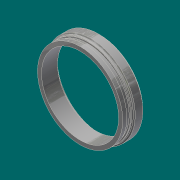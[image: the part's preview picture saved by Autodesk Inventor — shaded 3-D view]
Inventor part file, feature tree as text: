
AUTODESK INVENTOR PART (.ipt)
format: ipt  version: 2017.3 (Build 213256000, 256)  size: 171,520 bytes
history: native  units: in
note: dims shown in document units (in); Inventor stores cm internally (conversion verified against a paired STEP export)
features: revolve x1, chamfer x1, sketch x1
ambient origin geometry x8: Origin, YZ Plane, XZ Plane, XY Plane, X Axis, Y Axis, Z Axis, Center Point
bodies: Solid1 (feature_tree)
feature tree (3):
  revolve  "Revolution1"  [1 undecoded]
  chamfer  "Chamfer2"  Angle=90.0deg  [1 undecoded]
  sketch  "Sketch1"  dims[d0=15.625in d5=6.5in d6=90.0deg d13=16.75in d14=17.25in d16=1.75in d17=1.35in d18=0.0515in d19=0.0842in d20=0.0312in d21=0.125in d22=45.0deg d32=18.0in d33=0.4375in d34=0.1875in d35=0.0625in d36=0.5in d37=0.2577in d38=8.0in d39=0.25in d40=0.5in d41=30.0deg d42=0.5in]
note: 2 required parameter values undecoded (feature->parameter linkage not recoverable at this tier; creation-order binding heuristic only, values carry confidence <= 0.55)